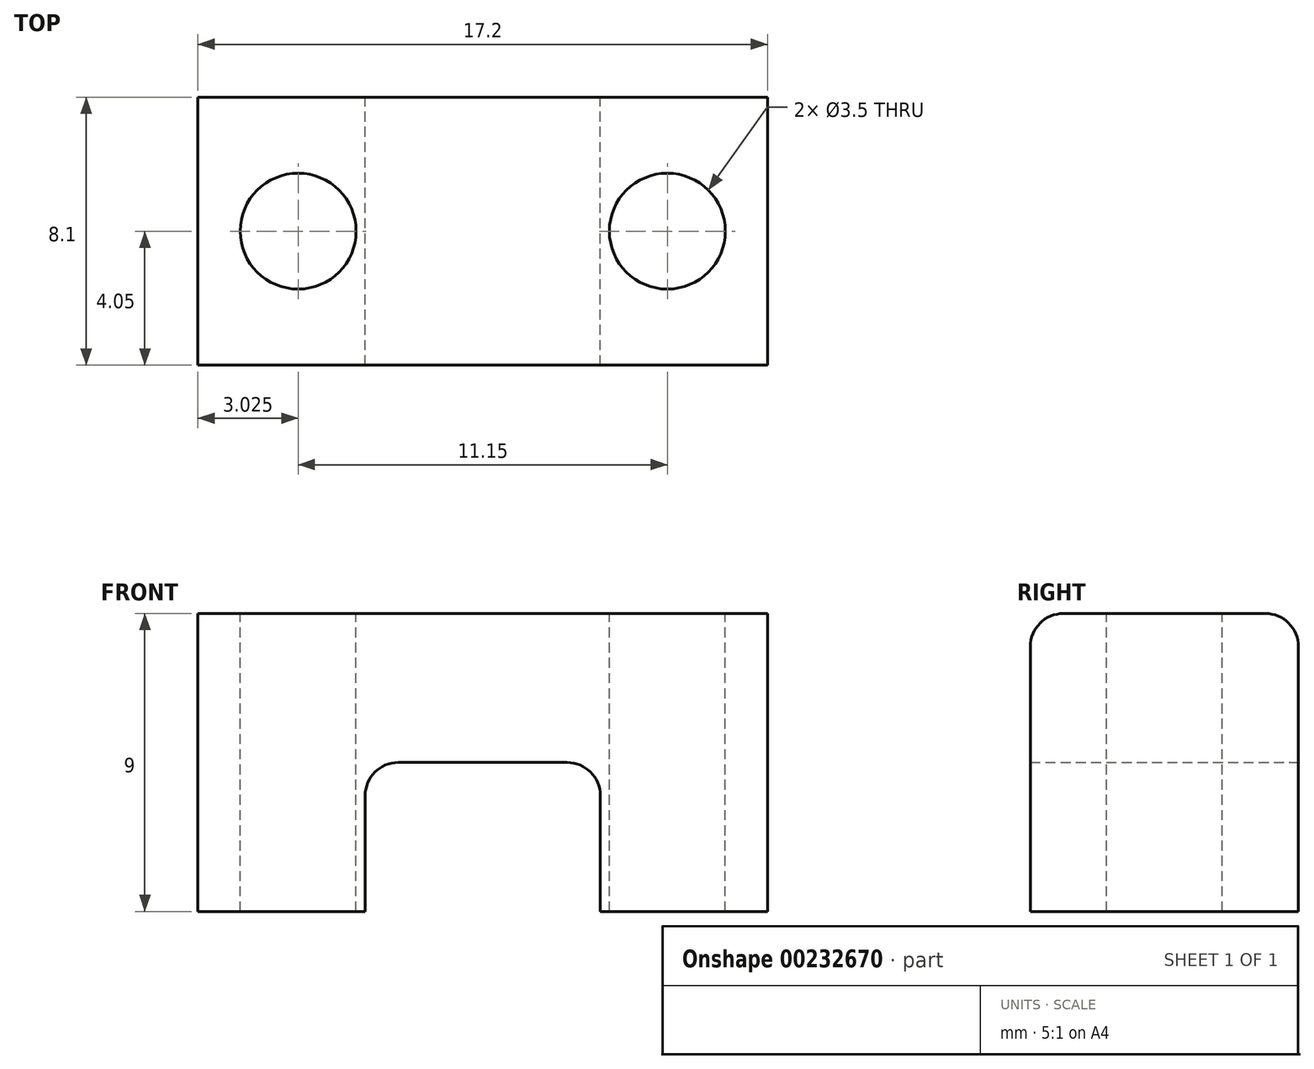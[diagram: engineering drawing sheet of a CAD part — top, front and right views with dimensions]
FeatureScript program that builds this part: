
annotation { "Feature Type Name" : "Feature", "Feature Type Description" : "" }
export const myFeature = defineFeature(function(context is Context, id is Id, definition is map)
    precondition{}
    {
        {
            var Q0;
            Q0=qCreatedBy(makeId("Front.planeOp"),FACE);
            var sketch = newSketch(context, id + "F0", { "sketchPlane" : qUnion([Q0])});
            skLineSegment(sketch, "E0", {"start": v(-8.6, 0) * mm, "end": v(-8.6, 9) * mm});
            skLineSegment(sketch, "E1", {"start": v(-8.6, 9) * mm, "end": v(8.6, 9) * mm});
            skLineSegment(sketch, "E2", {"start": v(8.6, 9) * mm, "end": v(8.6, 0) * mm});
            skLineSegment(sketch, "E3", {"start": v(8.6, 0) * mm, "end": v(3.55, 0) * mm});
            skLineSegment(sketch, "E4", {"start": v(3.55, 0) * mm, "end": v(3.55, 4.5) * mm});
            skLineSegment(sketch, "E5", {"start": v(3.55, 4.5) * mm, "end": v(-3.55, 4.5) * mm});
            skLineSegment(sketch, "E6", {"start": v(-3.55, 4.5) * mm, "end": v(-3.55, 0) * mm});
            skLineSegment(sketch, "E7", {"start": v(-3.55, 0) * mm, "end": v(-8.6, 0) * mm});
            skSolve(sketch);
        }
        {
            var Q0;
            Q0 = qSketchRegion(id + "F0", true);
            extrude(context, id + "F1", {"entities" : qUnion([Q0]), "depth" : 8.1 * mm});
        }
        {
            var Q0;
            Q0=makeQuery(id+"F1.opExtrude","SWEPT_FACE",FACE,{"disambiguationData":[OSD([sQuery(id+"F0.wireOp",EDGE,"E1")])]});
            var sketch = newSketch(context, id + "F2", { "sketchPlane" : qUnion([Q0])});
            skLineSegment(sketch, "E8", {"start": v(-12.2, -4.05) * mm, "end": v(13.93, -4.05) * mm, "construction": true});
            skPoint(sketch, "E8.startSnap0", {"position": v(-8.6, -4.05) * mm});
            skPoint(sketch, "E8.endSnap0", {"position": v(8.6, -4.05) * mm});
            skCircle(sketch, "E9", {"center": v(-5.58, -4.05) * mm, "radius": 1.75 * mm});
            skCircle(sketch, "E10", {"center": v(5.58, -4.05) * mm, "radius": 1.75 * mm});
            skSolve(sketch);
        }
        {
            var Q0;
            Q0 = qSketchRegion(id + "F2", true);
            extrude(context, id + "F3", {"entities" : qUnion([Q0]), "operationType" : NewBodyOperationType.REMOVE, "endBound" : BoundingType.THROUGH_ALL, "oppositeDirection" : true, "depth" : 25 * mm});
        }
        {
            var Q0;
            Q0=makeQuery(id+"F1.opExtrude","CAP_EDGE",EDGE,{"disambiguationData":[OSD([sQuery(id+"F0.wireOp",EDGE,"E1")])],"isStart":false});
            var Q1;
            Q1=makeQuery(id+"F1.opExtrude","CAP_EDGE",EDGE,{"disambiguationData":[OSD([sQuery(id+"F0.wireOp",EDGE,"E1")])],"isStart":true});
            var Q2;
            Q2=makeQuery(id+"F1.opExtrude","SWEPT_EDGE",EDGE,{"disambiguationData":[OSD([sQuery(id+"F0.wireOp",EDGE,"E5"),sQuery(id+"F0.wireOp",EDGE,"E6")])]});
            var Q3;
            Q3=makeQuery(id+"F1.opExtrude","SWEPT_EDGE",EDGE,{"disambiguationData":[OSD([sQuery(id+"F0.wireOp",EDGE,"E4"),sQuery(id+"F0.wireOp",EDGE,"E5")])]});
            fillet(context, id + "F4", {"entities" : qUnion([Q0, Q1, Q2, Q3]), "radius" : 1 * mm, "tangentPropagation" : true, "allowEdgeOverflow" : false});
        }
    });
